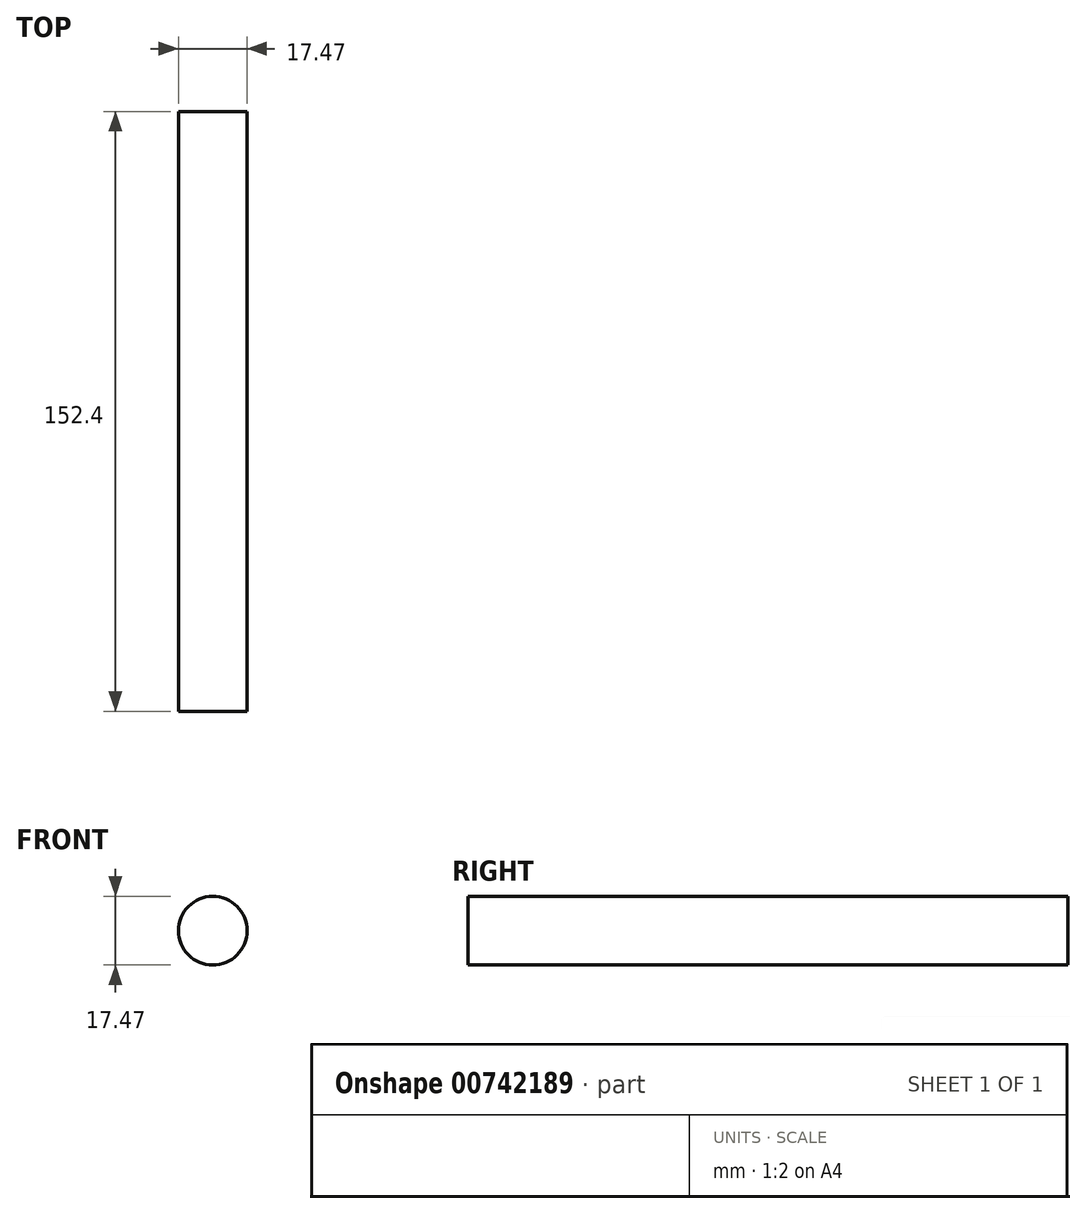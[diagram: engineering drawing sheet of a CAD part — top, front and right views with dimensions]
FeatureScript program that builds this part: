
annotation { "Feature Type Name" : "Feature", "Feature Type Description" : "" }
export const myFeature = defineFeature(function(context is Context, id is Id, definition is map)
    precondition{}
    {
        {
            var Q0;
            Q0=qCreatedBy(makeId("Front.planeOp"),FACE);
            var sketch = newSketch(context, id + "F0", { "sketchPlane" : qUnion([Q0])});
            skCircle(sketch, "E0", {"center": v(-15.42, -12.37) * mm, "radius": 8.73 * mm});
            skSolve(sketch);
        }
        {
            var Q0;
            Q0=makeQuery(id+"F0.imprint","IMPRINT",FACE,{"disambiguationData":[TD([[makeQuery(id+"F0.imprint","IMPRINT",EDGE,{"derivedFrom":sQuery(id+"F0.wireOp",EDGE,"E0")}),1.0]])]});
            extrude(context, id + "F1", {"entities" : qUnion([Q0]), "depth" : 152.4 * mm, "offsetDistance" : 25.4 * mm});
        }
    });
